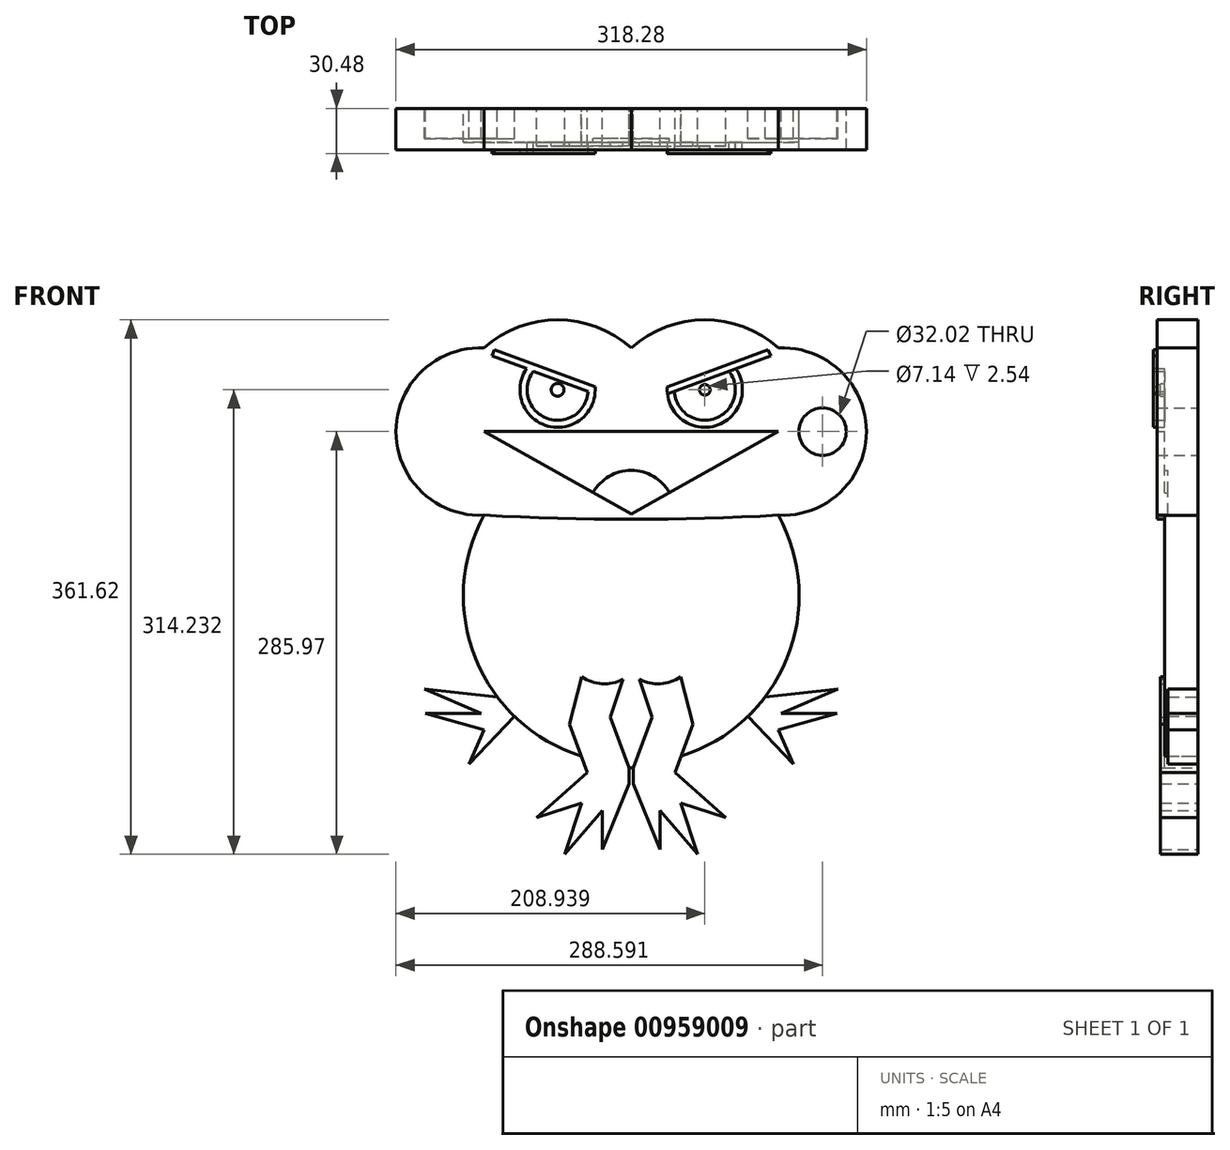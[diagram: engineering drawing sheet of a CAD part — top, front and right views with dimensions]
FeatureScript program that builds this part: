
annotation { "Feature Type Name" : "Feature", "Feature Type Description" : "" }
export const myFeature = defineFeature(function(context is Context, id is Id, definition is map)
    precondition{}
    {
        {
            var Q0;
            Q0=qCreatedBy(makeId("Front.planeOp"),FACE);
            var sketch = newSketch(context, id + "F0", { "sketchPlane" : qUnion([Q0])});
            skPoint(sketch, "E0.middle", {"position": v(0, 0) * mm});
            skPoint(sketch, "E0.right.end.orphan", {"position": v(-99.6, -56.52) * mm});
            skPoint(sketch, "E1.orphan", {"position": v(-99.6, 56.52) * mm});
            skLineSegment(sketch, "E2", {"start": v(0, 0) * mm, "end": v(99.6, 0) * mm});
            skArc(sketch, "E3", {"start": v(99.6, 56.52) * mm, "mid": v(49.8, 75.65) * mm, "end": v(0, 56.52) * mm});
            skArc(sketch, "E4", {"start": v(99.6, -56.52) * mm, "mid": v(159.14, 0) * mm, "end": v(99.6, 56.52) * mm});
            skLineSegment(sketch, "E5", {"start": v(0, -55.83) * mm, "end": v(99.6, 0) * mm});
            skArc(sketch, "E6", {"start": v(25.85, -41.34) * mm, "mid": v(14.98, -30.26) * mm, "end": v(0, -26.2) * mm});
            skLineSegment(sketch, "E7.MirrorCS", {"start": v(-24.53, 25.5) * mm, "end": v(-70.75, 42.66) * mm});
            skArc(sketch, "E8.MirrorCS", {"start": v(-25.85, -41.34) * mm, "mid": v(-14.98, -30.26) * mm, "end": v(0, -26.2) * mm});
            skArc(sketch, "E9.MirrorC", {"start": v(-24.45, 30.18) * mm, "mid": v(-56.41, 3.72) * mm, "end": v(-70.75, 42.66) * mm});
            skLineSegment(sketch, "E10.MirrorCS", {"start": v(0, 0) * mm, "end": v(-99.6, 0) * mm});
            skLineSegment(sketch, "E11.MirrorCS", {"start": v(0, -55.83) * mm, "end": v(-99.6, 0) * mm});
            skArc(sketch, "E12.MirrorCS", {"start": v(-99.6, -56.52) * mm, "mid": v(-159.14, 0) * mm, "end": v(-99.6, 56.52) * mm});
            skArc(sketch, "E13.MirrorCS", {"start": v(-99.6, 56.52) * mm, "mid": v(-49.8, 75.65) * mm, "end": v(0, 56.52) * mm});
            skCircle(sketch, "E14", {"center": v(-129.45, 0) * mm, "radius": 16.01 * mm});
            skCircle(sketch, "E15.MirrorC", {"center": v(129.45, 0) * mm, "radius": 16.01 * mm});
            skArc(sketch, "E16", {"start": v(-99.6, -56.52) * mm, "mid": v(0, -59.3) * mm, "end": v(99.6, -56.52) * mm});
            skArc(sketch, "E17", {"start": v(-66.07, 40.92) * mm, "mid": v(-56.98, 8.93) * mm, "end": v(-29.2, 27.23) * mm});
            skLineSegment(sketch, "E18", {"start": v(-67.75, 46.26) * mm, "end": v(-24.45, 30.18) * mm});
            skLineSegment(sketch, "E19.MirrorCS", {"start": v(24.53, 25.5) * mm, "end": v(70.75, 42.66) * mm});
            skArc(sketch, "E20.MirrorCS", {"start": v(66.07, 40.92) * mm, "mid": v(56.98, 8.93) * mm, "end": v(29.2, 27.23) * mm});
            skArc(sketch, "E21.MirrorCS", {"start": v(24.45, 30.18) * mm, "mid": v(56.41, 3.72) * mm, "end": v(70.75, 42.66) * mm});
            skCircle(sketch, "E22", {"center": v(-49.8, 28.26) * mm, "radius": 4.33 * mm});
            skCircle(sketch, "E23", {"center": v(49.8, 28.26) * mm, "radius": 3.57 * mm});
            skLineSegment(sketch, "E24", {"start": v(24.45, 30.18) * mm, "end": v(92.48, 55.44) * mm});
            skLineSegment(sketch, "E25", {"start": v(70.75, 42.66) * mm, "end": v(94.3, 51.4) * mm});
            skLineSegment(sketch, "E26", {"start": v(94.3, 51.4) * mm, "end": v(92.48, 55.44) * mm});
            skLineSegment(sketch, "E27.MirrorCS", {"start": v(-70.75, 42.66) * mm, "end": v(-94.3, 51.4) * mm});
            skLineSegment(sketch, "E28.MirrorCS", {"start": v(-24.45, 30.18) * mm, "end": v(-92.48, 55.44) * mm});
            skLineSegment(sketch, "E29.MirrorCS", {"start": v(-94.3, 51.4) * mm, "end": v(-92.48, 55.44) * mm});
            skLineSegment(sketch, "E30", {"start": v(1.5, -238.31) * mm, "end": v(19.61, -282.82) * mm});
            skLineSegment(sketch, "E31", {"start": v(19.61, -282.82) * mm, "end": v(19.61, -256.35) * mm});
            skLineSegment(sketch, "E32", {"start": v(19.61, -256.35) * mm, "end": v(44.82, -285.97) * mm});
            skLineSegment(sketch, "E33", {"start": v(44.82, -285.97) * mm, "end": v(33.48, -251.3) * mm});
            skLineSegment(sketch, "E34", {"start": v(33.48, -251.3) * mm, "end": v(64.03, -261.15) * mm});
            skLineSegment(sketch, "E35", {"start": v(64.03, -261.15) * mm, "end": v(29.6, -230.8) * mm});
            skLineSegment(sketch, "E36.MirrorCS", {"start": v(-1.5, -238.31) * mm, "end": v(-19.61, -282.82) * mm});
            skLineSegment(sketch, "E37.MirrorCS", {"start": v(-44.82, -285.97) * mm, "end": v(-33.48, -251.3) * mm});
            skLineSegment(sketch, "E38.MirrorCS", {"start": v(-19.61, -256.35) * mm, "end": v(-44.82, -285.97) * mm});
            skLineSegment(sketch, "E39.MirrorCS", {"start": v(-33.48, -251.3) * mm, "end": v(-64.03, -261.15) * mm});
            skLineSegment(sketch, "E40.MirrorCS", {"start": v(-19.61, -282.82) * mm, "end": v(-19.61, -256.35) * mm});
            skLineSegment(sketch, "E41.MirrorCS", {"start": v(-64.03, -261.15) * mm, "end": v(-29.6, -230.8) * mm});
            skArc(sketch, "E42", {"start": v(-99.6, -56.52) * mm, "mid": v(-105.3, -153.6) * mm, "end": v(-33.8, -219.5) * mm});
            skLineSegment(sketch, "E43", {"start": v(-90.7, -179.44) * mm, "end": v(-139.74, -174.07) * mm});
            skLineSegment(sketch, "E44", {"start": v(-139.74, -174.07) * mm, "end": v(-101.38, -190.8) * mm});
            skLineSegment(sketch, "E45", {"start": v(-101.38, -190.8) * mm, "end": v(-139.3, -190.8) * mm});
            skLineSegment(sketch, "E46", {"start": v(-139.3, -190.8) * mm, "end": v(-99.44, -201.67) * mm});
            skLineSegment(sketch, "E47", {"start": v(-99.44, -201.67) * mm, "end": v(-109.56, -224.8) * mm});
            skLineSegment(sketch, "E48", {"start": v(-109.56, -224.8) * mm, "end": v(-78.99, -192.68) * mm});
            skLineSegment(sketch, "E49.MirrorCS", {"start": v(139.74, -174.07) * mm, "end": v(101.38, -190.8) * mm});
            skLineSegment(sketch, "E50.MirrorCS", {"start": v(139.3, -190.8) * mm, "end": v(99.44, -201.67) * mm});
            skLineSegment(sketch, "E51.MirrorCS", {"start": v(90.7, -179.44) * mm, "end": v(139.74, -174.07) * mm});
            skLineSegment(sketch, "E52.MirrorCS", {"start": v(101.38, -190.8) * mm, "end": v(139.3, -190.8) * mm});
            skLineSegment(sketch, "E53.MirrorCS", {"start": v(109.56, -224.8) * mm, "end": v(78.99, -192.68) * mm});
            skLineSegment(sketch, "E54.MirrorCS", {"start": v(99.44, -201.67) * mm, "end": v(109.56, -224.8) * mm});
            skArc(sketch, "E55.trimOffspring", {"start": v(31.3, -220.25) * mm, "mid": v(104.81, -154.8) * mm, "end": v(99.6, -56.52) * mm});
            skLineSegment(sketch, "E56", {"start": v(-1.5, -227.44) * mm, "end": v(-1.5, -238.31) * mm});
            skLineSegment(sketch, "E57", {"start": v(1.5, -227.44) * mm, "end": v(1.5, -238.31) * mm});
            skLineSegment(sketch, "E58", {"start": v(-1.5, -227.44) * mm, "end": v(1.5, -227.44) * mm});
            skLineSegment(sketch, "E59", {"start": v(-1.5, -227.44) * mm, "end": v(-14.23, -193.25) * mm});
            skLineSegment(sketch, "E60", {"start": v(-14.23, -193.25) * mm, "end": v(-5.64, -167.5) * mm});
            skLineSegment(sketch, "E61", {"start": v(-29.6, -230.8) * mm, "end": v(-41.83, -197.9) * mm});
            skLineSegment(sketch, "E62", {"start": v(-41.83, -197.9) * mm, "end": v(-33.47, -165.94) * mm});
            skLineSegment(sketch, "E63.MirrorCS", {"start": v(14.23, -193.25) * mm, "end": v(5.64, -167.5) * mm});
            skLineSegment(sketch, "E64.MirrorCS", {"start": v(1.5, -227.44) * mm, "end": v(14.23, -193.25) * mm});
            skLineSegment(sketch, "E65.MirrorCS", {"start": v(29.6, -230.8) * mm, "end": v(41.83, -197.9) * mm});
            skLineSegment(sketch, "E66.MirrorCS", {"start": v(41.83, -197.9) * mm, "end": v(33.47, -165.94) * mm});
            skArc(sketch, "E67", {"start": v(-33.47, -165.94) * mm, "mid": v(-19.78, -170.61) * mm, "end": v(-5.64, -167.5) * mm});
            skArc(sketch, "E68.MirrorCS", {"start": v(33.47, -165.94) * mm, "mid": v(19.78, -170.61) * mm, "end": v(5.64, -167.5) * mm});
            skSolve(sketch);
        }
        {
            var Q0;
            {var subQ1=sQuery(id+"F0.wireOp",EDGE,"E2");Q0=makeQuery(id+"F0.imprint","IMPRINT",FACE,{"disambiguationData":[TD([[makeQuery(id+"F0.imprint","IMPRINT",EDGE,{"derivedFrom":subQ1}),1.0]])]});}
            extrude(context, id + "F1", {"entities" : qUnion([Q0]), "depth" : 25.4 * mm, "offsetDistance" : 25.4 * mm});
        }
        {
            var Q0;
            Q0=makeQuery(id+"F0.imprint","IMPRINT",FACE,{"disambiguationData":[TD([[makeQuery(id+"F0.imprint","IMPRINT",EDGE,{"derivedFrom":sQuery(id+"F0.wireOp",EDGE,"E14")}),1.0]])]});
            var Q1;
            Q1=makeQuery(id+"F0.imprint","IMPRINT",FACE,{"disambiguationData":[TD([[makeQuery(id+"F0.imprint","IMPRINT",EDGE,{"derivedFrom":sQuery(id+"F0.wireOp",EDGE,"E15.MirrorC")}),-1.0]])]});
            extrude(context, id + "F2", {"entities" : qUnion([Q0, Q1]), "operationType" : NewBodyOperationType.ADD, "depth" : 27.94 * mm, "offsetDistance" : 25.4 * mm});
        }
        {
            var Q0;
            {var subQ3=sQuery(id+"F0.wireOp",EDGE,"E2");Q0=makeQuery(id+"F0.imprint","IMPRINT",FACE,{"disambiguationData":[TD([[makeQuery(id+"F0.imprint","IMPRINT",EDGE,{"derivedFrom":subQ3}),-1.0]])]});}
            extrude(context, id + "F3", {"entities" : qUnion([Q0]), "operationType" : NewBodyOperationType.ADD, "depth" : 22.86 * mm, "offsetDistance" : 25.4 * mm});
        }
        {
            var Q0;
            {var subQ3=sQuery(id+"F0.wireOp",EDGE,"E6");Q0=makeQuery(id+"F0.imprint","IMPRINT",FACE,{"disambiguationData":[TD([[makeQuery(id+"F0.imprint","IMPRINT",EDGE,{"derivedFrom":subQ3}),1.0]])]});}
            extrude(context, id + "F4", {"entities" : qUnion([Q0]), "operationType" : NewBodyOperationType.ADD, "depth" : 20.32 * mm, "offsetDistance" : 25.4 * mm});
        }
        {
            var Q0;
            {var subQ5=sQuery(id+"F0.wireOp",EDGE,"E27.MirrorCS");Q0=makeQuery(id+"F0.imprint","IMPRINT",FACE,{"disambiguationData":[TD([[makeQuery(id+"F0.imprint","IMPRINT",EDGE,{"derivedFrom":subQ5}),-1.0]])]});}
            var Q1;
            {var subQ3=sQuery(id+"F0.wireOp",EDGE,"E24");Q1=makeQuery(id+"F0.imprint","IMPRINT",FACE,{"disambiguationData":[TD([[makeQuery(id+"F0.imprint","IMPRINT",EDGE,{"derivedFrom":subQ3}),-1.0]])]});}
            extrude(context, id + "F5", {"entities" : qUnion([Q0, Q1]), "operationType" : NewBodyOperationType.ADD, "depth" : 30.48 * mm, "offsetDistance" : 25.4 * mm});
        }
        {
            var Q0;
            {var subQ0=sQuery(id+"F0.wireOp",EDGE,"E17");Q0=makeQuery(id+"F0.imprint","IMPRINT",FACE,{"disambiguationData":[TD([[makeQuery(id+"F0.imprint","IMPRINT",EDGE,{"derivedFrom":subQ0}),1.0]])]});}
            var Q1;
            {var subQ0=sQuery(id+"F0.wireOp",EDGE,"E20.MirrorCS");Q1=makeQuery(id+"F0.imprint","IMPRINT",FACE,{"disambiguationData":[TD([[makeQuery(id+"F0.imprint","IMPRINT",EDGE,{"derivedFrom":subQ0}),-1.0]])]});}
            extrude(context, id + "F6", {"entities" : qUnion([Q0, Q1]), "operationType" : NewBodyOperationType.ADD, "depth" : 22.86 * mm, "offsetDistance" : 25.4 * mm});
        }
        {
            var Q0;
            {var subQ3=sQuery(id+"F0.wireOp",EDGE,"E17");Q0=makeQuery(id+"F0.imprint","IMPRINT",FACE,{"disambiguationData":[TD([[makeQuery(id+"F0.imprint","IMPRINT",EDGE,{"derivedFrom":subQ3}),-1.0]])]});}
            var Q1;
            {var subQ3=sQuery(id+"F0.wireOp",EDGE,"E20.MirrorCS");Q1=makeQuery(id+"F0.imprint","IMPRINT",FACE,{"disambiguationData":[TD([[makeQuery(id+"F0.imprint","IMPRINT",EDGE,{"derivedFrom":subQ3}),1.0]])]});}
            extrude(context, id + "F7", {"entities" : qUnion([Q0, Q1]), "operationType" : NewBodyOperationType.ADD, "depth" : 27.94 * mm, "offsetDistance" : 25.4 * mm});
        }
        {
            var Q0;
            Q0=makeQuery(id+"F0.imprint","IMPRINT",FACE,{"disambiguationData":[TD([[makeQuery(id+"F0.imprint","IMPRINT",EDGE,{"derivedFrom":sQuery(id+"F0.wireOp",EDGE,"E22")}),1.0]])]});
            var Q1;
            Q1=makeQuery(id+"F0.imprint","IMPRINT",FACE,{"disambiguationData":[TD([[makeQuery(id+"F0.imprint","IMPRINT",EDGE,{"derivedFrom":sQuery(id+"F0.wireOp",EDGE,"E23")}),1.0]])]});
            extrude(context, id + "F8", {"entities" : qUnion([Q0, Q1]), "operationType" : NewBodyOperationType.ADD, "depth" : 25.4 * mm, "offsetDistance" : 25.4 * mm});
        }
        {
            var Q0;
            {var subQ5=sQuery(id+"F0.wireOp",EDGE,"E16");Q0=makeQuery(id+"F0.imprint","IMPRINT",FACE,{"disambiguationData":[TD([[makeQuery(id+"F0.imprint","IMPRINT",EDGE,{"derivedFrom":subQ5}),-1.0]])]});}
            extrude(context, id + "F9", {"entities" : qUnion([Q0]), "operationType" : NewBodyOperationType.ADD, "depth" : 22.86 * mm, "offsetDistance" : 25.4 * mm});
        }
        {
            var Q0;
            Q0=makeQuery(id+"F0.imprint","IMPRINT",FACE,{"disambiguationData":[TD([[makeQuery(id+"F0.imprint","IMPRINT",EDGE,{"derivedFrom":sQuery(id+"F0.wireOp",EDGE,"E36.MirrorCS")}),-1.0]])]});
            var Q1;
            Q1=makeQuery(id+"F0.imprint","IMPRINT",FACE,{"disambiguationData":[TD([[makeQuery(id+"F0.imprint","IMPRINT",EDGE,{"derivedFrom":sQuery(id+"F0.wireOp",EDGE,"E30")}),1.0]])]});
            extrude(context, id + "F10", {"entities" : qUnion([Q0, Q1]), "operationType" : NewBodyOperationType.ADD, "depth" : 25.4 * mm, "offsetDistance" : 25.4 * mm});
        }
        {
            var Q0;
            {var subQ0=sQuery(id+"F0.wireOp",EDGE,"E43");Q0=makeQuery(id+"F0.imprint","IMPRINT",FACE,{"disambiguationData":[TD([[makeQuery(id+"F0.imprint","IMPRINT",EDGE,{"derivedFrom":subQ0}),1.0]])]});}
            var Q1;
            Q1=makeQuery(id+"F0.imprint","IMPRINT",FACE,{"disambiguationData":[TD([[makeQuery(id+"F0.imprint","IMPRINT",EDGE,{"derivedFrom":sQuery(id+"F0.wireOp",EDGE,"E49.MirrorCS")}),-1.0]])]});
            extrude(context, id + "F11", {"entities" : qUnion([Q0, Q1]), "operationType" : NewBodyOperationType.ADD, "depth" : 20.32 * mm, "offsetDistance" : 25.4 * mm});
        }
    });
